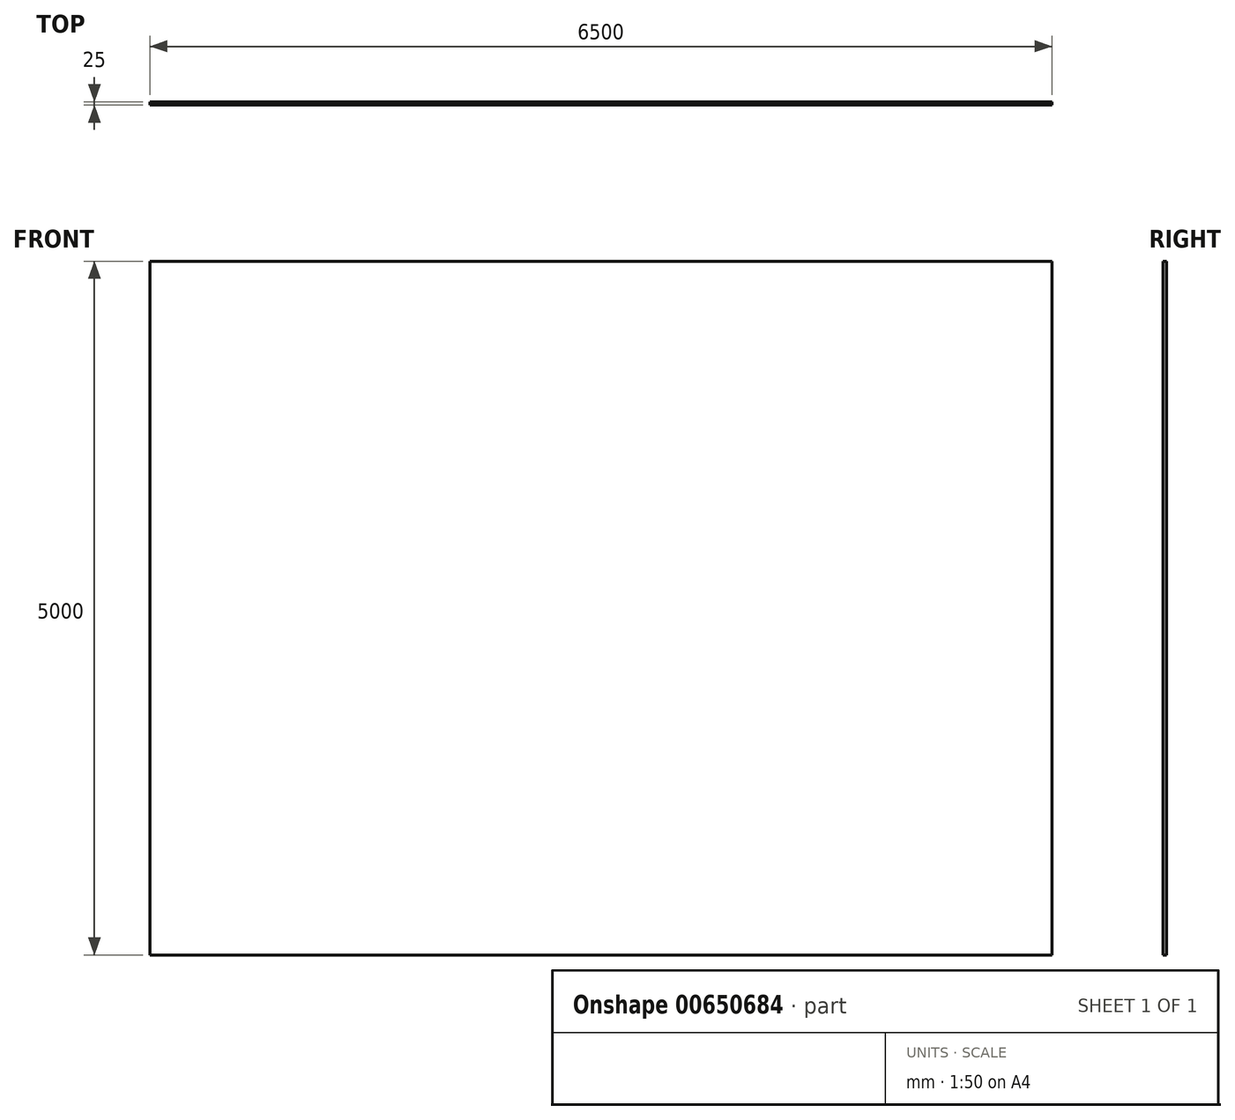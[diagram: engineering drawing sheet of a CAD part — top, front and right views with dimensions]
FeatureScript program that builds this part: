
annotation { "Feature Type Name" : "Feature", "Feature Type Description" : "" }
export const myFeature = defineFeature(function(context is Context, id is Id, definition is map)
    precondition{}
    {
        {
            var Q0;
            Q0=qCreatedBy(makeId("Front.planeOp"),FACE);
            var sketch = newSketch(context, id + "F0", { "sketchPlane" : qUnion([Q0])});
            skLineSegment(sketch, "E0.bottom", {"start": v(-2496.64, 2017.04) * mm, "end": v(4003.36, 2017.04) * mm});
            skLineSegment(sketch, "E0.top", {"start": v(-2496.64, -2982.96) * mm, "end": v(4003.36, -2982.96) * mm});
            skLineSegment(sketch, "E0.left", {"start": v(-2496.64, 2017.04) * mm, "end": v(-2496.64, -2982.96) * mm});
            skLineSegment(sketch, "E0.right", {"start": v(4003.36, 2017.04) * mm, "end": v(4003.36, -2982.96) * mm});
            skSolve(sketch);
        }
        {
            var Q0;
            Q0=makeQuery(id+"F0.imprint","IMPRINT",FACE,{"disambiguationData":[TD([[makeQuery(id+"F0.imprint","IMPRINT",EDGE,{"derivedFrom":sQuery(id+"F0.wireOp",EDGE,"E0.bottom")}),-1.0]])]});
            extrude(context, id + "F1", {"entities" : qUnion([Q0]), "depth" : 25 * mm, "offsetDistance" : 25 * mm});
        }
    });
